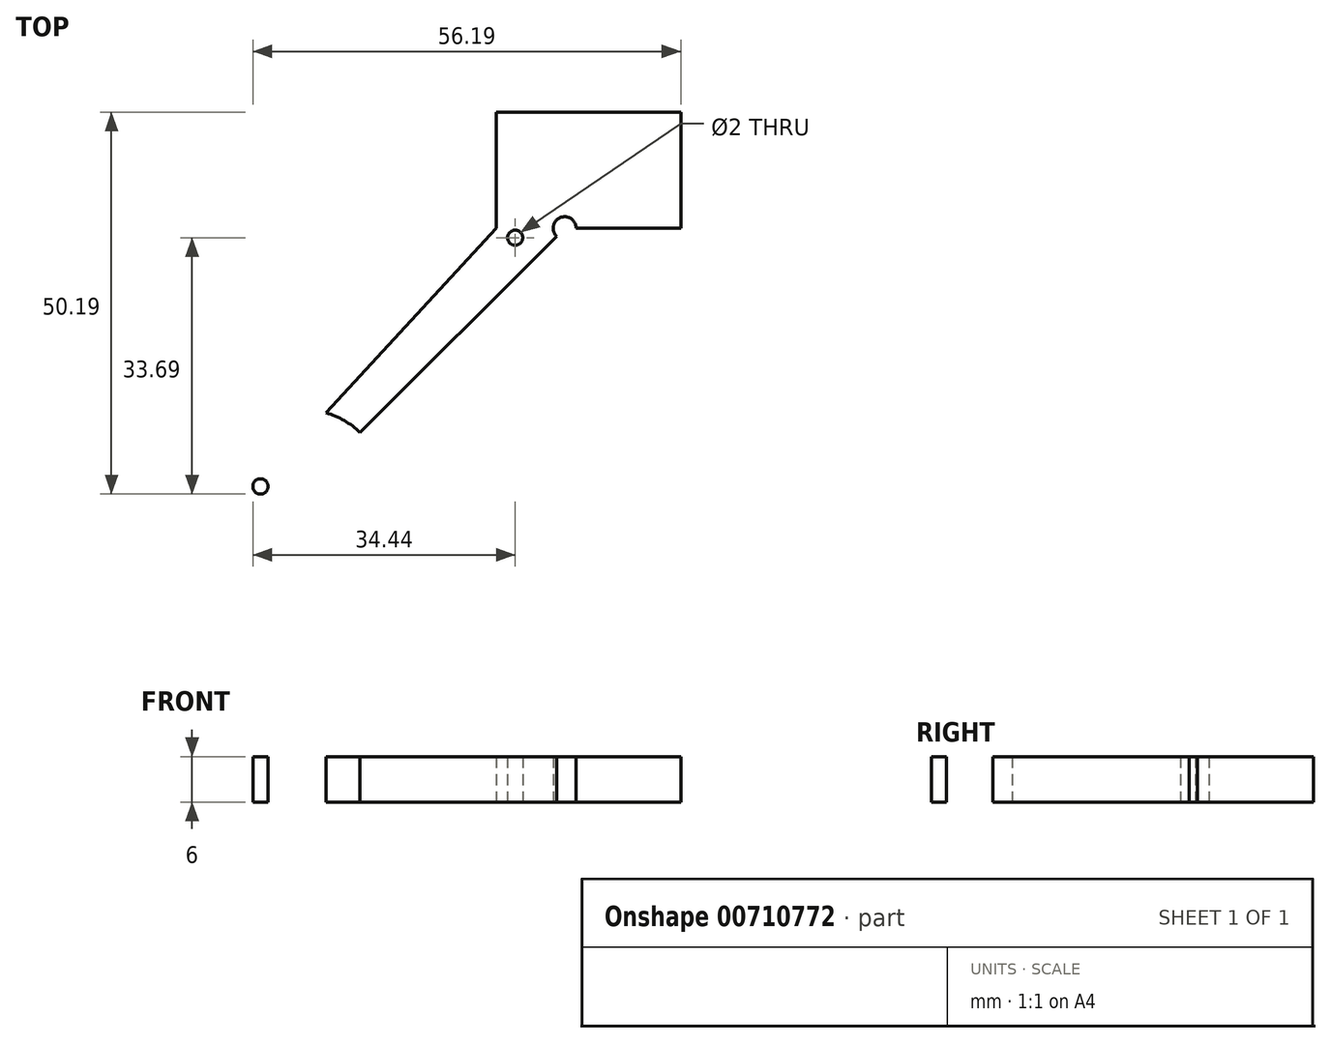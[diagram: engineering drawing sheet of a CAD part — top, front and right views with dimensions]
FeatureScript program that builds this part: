
annotation { "Feature Type Name" : "Feature", "Feature Type Description" : "" }
export const myFeature = defineFeature(function(context is Context, id is Id, definition is map)
    precondition{}
    {
        {
            var Q0;
            Q0=qCreatedBy(makeId("Top.planeOp"),FACE);
            var sketch = newSketch(context, id + "F0", { "sketchPlane" : qUnion([Q0])});
            skLineSegment(sketch, "E0.top", {"start": v(-15.25, -15.25) * mm, "end": v(-24.25, -15.25) * mm});
            skCircle(sketch, "E1.MirrorC", {"center": v(-55.2, -49.2) * mm, "radius": 1 * mm});
            skCircle(sketch, "E2.MirrorC", {"center": v(-43.2, -49.2) * mm, "radius": 1 * mm});
            skCircle(sketch, "E3.MirrorC", {"center": v(-49.2, -55.2) * mm, "radius": 1 * mm});
            skCircle(sketch, "E4.MirrorC", {"center": v(-49.2, -43.2) * mm, "radius": 1 * mm});
            skLineSegment(sketch, "E5.MirrorCS", {"start": v(-39.53, -46.6) * mm, "end": v(-8.18, -15.25) * mm});
            skLineSegment(sketch, "E6.MirrorCS", {"start": v(-46.6, -39.53) * mm, "end": v(-24.25, -15.25) * mm});
            skCircle(sketch, "E7.MirrorC", {"center": v(-49.2, -49.2) * mm, "radius": 10 * mm});
            skCircle(sketch, "E8.MirrorC", {"center": v(-49.2, -49.2) * mm, "radius": 2.5 * mm});
            skCircle(sketch, "E9", {"center": v(-15.25, -15.25) * mm, "radius": 1.5 * mm});
            skLineSegment(sketch, "E10", {"start": v(-24.25, -16.5) * mm, "end": v(-21.75, -16.5) * mm});
            skCircle(sketch, "E11", {"center": v(-21.75, -16.5) * mm, "radius": 1 * mm});
            skLineSegment(sketch, "E12.bottom", {"start": v(-24.25, -15.25) * mm, "end": v(0, -15.25) * mm});
            skLineSegment(sketch, "E12.top", {"start": v(-24.25, 0) * mm, "end": v(0, 0) * mm});
            skLineSegment(sketch, "E12.left", {"start": v(-24.25, -15.25) * mm, "end": v(-24.25, 0) * mm});
            skLineSegment(sketch, "E12.right", {"start": v(0, -15.25) * mm, "end": v(0, 0) * mm});
            skLineSegment(sketch, "E13", {"start": v(-49.2, -49.2) * mm, "end": v(-39.2, -49.2) * mm});
            skLineSegment(sketch, "E14", {"start": v(-39.2, -49.2) * mm, "end": v(-49.2, -49.2) * mm});
            skLineSegment(sketch, "E15", {"start": v(-59.2, -49.2) * mm, "end": v(-49.2, -49.2) * mm});
            skLineSegment(sketch, "E16", {"start": v(-49.2, -39.2) * mm, "end": v(-49.2, -59.2) * mm});
            skLineSegment(sketch, "E17", {"start": v(-15.25, -15.25) * mm, "end": v(-49.2, -49.2) * mm});
            skSolve(sketch);
        }
        {
            var Q0;
            Q0=makeQuery(id+"F0.imprint","IMPRINT",FACE,{"disambiguationData":[TD([[makeQuery(id+"F0.imprint","IMPRINT",EDGE,{"derivedFrom":sQuery(id+"F0.wireOp",EDGE,"2fc15603-6939-42b3-9b3e-9790c157a10a0.MirrorC")}),1.0]])]});
            var Q1;
            {var subQ5=sQuery(id+"F0.wireOp",EDGE,"2fc15603-6939-42b3-9b3e-9790c157a10a33.MirrorCS");Q1=makeQuery(id+"F0.imprint","IMPRINT",FACE,{"disambiguationData":[TD([[makeQuery(id+"F0.imprint","IMPRINT",EDGE,{"derivedFrom":subQ5}),-1.0]])]});}
            var Q2;
            {var subQ0=sQuery(id+"F0.wireOp",EDGE,"2fc15603-6939-42b3-9b3e-9790c157a10a26.MirrorCS");var subQ1=sQuery(id+"F0.wireOp",EDGE,"BjklgQHF-2lCu-BJus-xYrG-jcty17bZJsR9.bottom");var subQ2=makeQuery(id+"F0.imprint","INTERSECT",VERTEX,{"derivedFrom":[subQ1,subQ0]});Q2=makeQuery(id+"F0.imprint","IMPRINT",FACE,{"disambiguationData":[TD([[makeQuery(id+"F0.imprint","IMPRINT",EDGE,{"disambiguationData":[TD([[subQ2,-1.0]])],"derivedFrom":subQ1}),1.0]])]});}
            var Q3;
            {var subQ1=sQuery(id+"F0.wireOp",EDGE,"2fc15603-6939-42b3-9b3e-9790c157a10a22.MirrorCS");var subQ3=sQuery(id+"F0.wireOp",EDGE,"O8ek5n8F-vqc0-MOGU-3nzg-OkgxkjxWgx8A");var subQ4=makeQuery(id+"F0.imprint","INTERSECT",VERTEX,{"derivedFrom":[subQ1,subQ3]});Q3=makeQuery(id+"F0.imprint","IMPRINT",FACE,{"disambiguationData":[TD([[makeQuery(id+"F0.imprint","IMPRINT",EDGE,{"disambiguationData":[TD([[subQ4,1.0]])],"derivedFrom":subQ3}),-1.0]])]});}
            var Q4;
            {var subQ0=sQuery(id+"F0.wireOp",EDGE,"BjklgQHF-2lCu-BJus-xYrG-jcty17bZJsR9.bottom");var subQ8=makeQuery(id+"F0.imprint","INTERSECT",VERTEX,{"derivedFrom":[subQ0,sQuery(id+"F0.wireOp",EDGE,"T8tqe1wF-UkRa-UTp3-tCxK-rj2eIQjL2TSv")]});Q4=makeQuery(id+"F0.imprint","IMPRINT",FACE,{"disambiguationData":[TD([[makeQuery(id+"F0.imprint","IMPRINT",EDGE,{"disambiguationData":[TD([[subQ8,1.0]])],"derivedFrom":subQ0}),-1.0]])]});}
            var Q5;
            {var subQ3=sQuery(id+"F0.wireOp",EDGE,"QD21J1TR-R4I8-fKPh-C4il-LhPoGl2EDAA3");Q5=makeQuery(id+"F0.imprint","IMPRINT",FACE,{"disambiguationData":[TD([[makeQuery(id+"F0.imprint","IMPRINT",EDGE,{"derivedFrom":subQ3}),1.0]])]});}
            var Q6;
            Q6=makeQuery(id+"F0.imprint","IMPRINT",FACE,{"disambiguationData":[TD([[makeQuery(id+"F0.imprint","IMPRINT",EDGE,{"derivedFrom":sQuery(id+"F0.wireOp",EDGE,"G2xj0Bxy-JqKr-VXiR-P4dS-C8p4XoVfQqo2")}),-1.0]])]});
            var Q7;
            {var subQ1=sQuery(id+"F0.wireOp",EDGE,"E0.bottom");var subQ3=sQuery(id+"F0.wireOp",EDGE,"PJjClM9O-XOP3-8SZ1-1YEl-zbY6ReYBc9Jh");var subQ4=makeQuery(id+"F0.imprint","INTERSECT",VERTEX,{"derivedFrom":[subQ1,subQ3]});Q7=makeQuery(id+"F0.imprint","IMPRINT",FACE,{"disambiguationData":[TD([[makeQuery(id+"F0.imprint","IMPRINT",EDGE,{"disambiguationData":[TD([[subQ4,-1.0]])],"derivedFrom":subQ3}),-1.0]])]});}
            var Q8;
            {var subQ5=sQuery(id+"F0.wireOp",EDGE,"BjklgQHF-2lCu-BJus-xYrG-jcty17bZJsR9.bottom");var subQ7=sQuery(id+"F0.wireOp",EDGE,"T8tqe1wF-UkRa-UTp3-tCxK-rj2eIQjL2TSv");var subQ8=makeQuery(id+"F0.imprint","INTERSECT",VERTEX,{"derivedFrom":[subQ5,subQ7]});Q8=makeQuery(id+"F0.imprint","IMPRINT",FACE,{"disambiguationData":[TD([[makeQuery(id+"F0.imprint","IMPRINT",EDGE,{"disambiguationData":[TD([[subQ8,1.0]])],"derivedFrom":subQ5}),1.0]])]});}
            var Q9;
            {var subQ3=sQuery(id+"F0.wireOp",EDGE,"E0.left");var subQ7=sQuery(id+"F0.wireOp",EDGE,"PJjClM9O-XOP3-8SZ1-1YEl-zbY6ReYBc9Jh");var subQ9=makeQuery(id+"F0.imprint","INTERSECT",VERTEX,{"derivedFrom":[subQ3,subQ7]});Q9=makeQuery(id+"F0.imprint","IMPRINT",FACE,{"disambiguationData":[TD([[makeQuery(id+"F0.imprint","IMPRINT",EDGE,{"disambiguationData":[TD([[subQ9,-1.0]])],"derivedFrom":subQ3}),-1.0]])]});}
            var Q10;
            {var subQ0=sQuery(id+"F0.wireOp",EDGE,"PJjClM9O-XOP3-8SZ1-1YEl-zbY6ReYBc9Jh");var subQ1=sQuery(id+"F0.wireOp",EDGE,"E0.left");var subQ2=makeQuery(id+"F0.imprint","INTERSECT",VERTEX,{"derivedFrom":[subQ1,subQ0]});Q10=makeQuery(id+"F0.imprint","IMPRINT",FACE,{"disambiguationData":[TD([[makeQuery(id+"F0.imprint","IMPRINT",EDGE,{"disambiguationData":[TD([[subQ2,-1.0]])],"derivedFrom":subQ1}),1.0]])]});}
            var Q11;
            {var subQ1=sQuery(id+"F0.wireOp",EDGE,"E0.left");var subQ9=sQuery(id+"F0.wireOp",EDGE,"4uT9bfEZ-qlL9-jcBX-Nhsu-rmtl1X7BlQzy");var subQ11=makeQuery(id+"F0.imprint","INTERSECT",VERTEX,{"derivedFrom":[subQ1,subQ9]});Q11=makeQuery(id+"F0.imprint","IMPRINT",FACE,{"disambiguationData":[TD([[makeQuery(id+"F0.imprint","IMPRINT",EDGE,{"disambiguationData":[TD([[subQ11,-1.0]])],"derivedFrom":subQ1}),1.0]])]});}
            var Q12;
            {var subQ0=sQuery(id+"F0.wireOp",EDGE,"4uT9bfEZ-qlL9-jcBX-Nhsu-rmtl1X7BlQzy");var subQ3=sQuery(id+"F0.wireOp",EDGE,"E0.left");var subQ4=makeQuery(id+"F0.imprint","INTERSECT",VERTEX,{"derivedFrom":[subQ3,subQ0]});Q12=makeQuery(id+"F0.imprint","IMPRINT",FACE,{"disambiguationData":[TD([[makeQuery(id+"F0.imprint","IMPRINT",EDGE,{"disambiguationData":[TD([[subQ4,-1.0]])],"derivedFrom":subQ3}),-1.0]])]});}
            var Q13;
            {var subQ0=sQuery(id+"F0.wireOp",EDGE,"zzauZid5-o7Uc-fnxz-2Q5N-lc55jAUrYsHn");Q13=makeQuery(id+"F0.imprint","IMPRINT",FACE,{"disambiguationData":[TD([[makeQuery(id+"F0.imprint","IMPRINT",EDGE,{"derivedFrom":subQ0}),-1.0]])]});}
            var Q14;
            {var subQ0=sQuery(id+"F0.wireOp",EDGE,"oEed2lwB-LAN2-I5ee-bfS7-ysMyHjfk99YW");Q14=makeQuery(id+"F0.imprint","IMPRINT",FACE,{"disambiguationData":[TD([[makeQuery(id+"F0.imprint","IMPRINT",EDGE,{"derivedFrom":subQ0}),-1.0]])]});}
            var Q15;
            {var subQ3=sQuery(id+"F0.wireOp",EDGE,"ZsRWKTD2-uWTc-TLXd-d7Hk-2En77BC8SWwa");Q15=makeQuery(id+"F0.imprint","IMPRINT",FACE,{"disambiguationData":[TD([[makeQuery(id+"F0.imprint","IMPRINT",EDGE,{"derivedFrom":subQ3}),1.0]])]});}
            var Q16;
            {var subQ0=sQuery(id+"F0.wireOp",EDGE,"2fc15603-6939-42b3-9b3e-9790c157a10a34.MirrorCS");Q16=makeQuery(id+"F0.imprint","IMPRINT",FACE,{"disambiguationData":[TD([[makeQuery(id+"F0.imprint","IMPRINT",EDGE,{"derivedFrom":subQ0}),-1.0]])]});}
            var Q17;
            Q17=makeQuery(id+"F0.imprint","IMPRINT",FACE,{"disambiguationData":[TD([[makeQuery(id+"F0.imprint","IMPRINT",EDGE,{"derivedFrom":sQuery(id+"F0.wireOp",EDGE,"2fc15603-6939-42b3-9b3e-9790c157a10a1.MirrorC")}),-1.0]])]});
            var Q18;
            {var subQ1=sQuery(id+"F0.wireOp",EDGE,"BjklgQHF-2lCu-BJus-xYrG-jcty17bZJsR9.top");var subQ7=sQuery(id+"F0.wireOp",EDGE,"E5.MirrorCS");var subQ8=makeQuery(id+"F0.imprint","INTERSECT",VERTEX,{"derivedFrom":[subQ1,subQ7]});Q18=makeQuery(id+"F0.imprint","IMPRINT",FACE,{"disambiguationData":[TD([[makeQuery(id+"F0.imprint","IMPRINT",EDGE,{"disambiguationData":[TD([[subQ8,1.0]])],"derivedFrom":subQ1}),-1.0]])]});}
            var Q19;
            {var subQ5=sQuery(id+"F0.wireOp",EDGE,"E6.MirrorCS");Q19=makeQuery(id+"F0.imprint","IMPRINT",FACE,{"disambiguationData":[TD([[makeQuery(id+"F0.imprint","IMPRINT",EDGE,{"derivedFrom":subQ5}),-1.0]])]});}
            var Q20;
            Q20=makeQuery(id+"F0.imprint","IMPRINT",FACE,{"disambiguationData":[TD([[makeQuery(id+"F0.imprint","IMPRINT",EDGE,{"derivedFrom":sQuery(id+"F0.wireOp",EDGE,"E1.MirrorC")}),1.0]])]});
            var Q21;
            {var subQ0=sQuery(id+"F0.wireOp",EDGE,"BjklgQHF-2lCu-BJus-xYrG-jcty17bZJsR9.top");var subQ4=makeQuery(id+"F0.imprint","INTERSECT",VERTEX,{"derivedFrom":[subQ0,sQuery(id+"F0.wireOp",EDGE,"E5.MirrorCS")]});Q21=makeQuery(id+"F0.imprint","IMPRINT",FACE,{"disambiguationData":[TD([[makeQuery(id+"F0.imprint","IMPRINT",EDGE,{"disambiguationData":[TD([[subQ4,1.0]])],"derivedFrom":subQ0}),1.0]])]});}
            var Q22;
            {var subQ1=sQuery(id+"F0.wireOp",EDGE,"2fc15603-6939-42b3-9b3e-9790c157a10a29.MirrorCS");var subQ3=sQuery(id+"F0.wireOp",EDGE,"nAFaoFor-0JIV-fJh0-xI6d-kOEGwFpFNsGw");var subQ4=makeQuery(id+"F0.imprint","INTERSECT",VERTEX,{"derivedFrom":[subQ1,subQ3]});Q22=makeQuery(id+"F0.imprint","IMPRINT",FACE,{"disambiguationData":[TD([[makeQuery(id+"F0.imprint","IMPRINT",EDGE,{"disambiguationData":[TD([[subQ4,-1.0]])],"derivedFrom":subQ3}),-1.0]])]});}
            var Q23;
            {var subQ1=sQuery(id+"F0.wireOp",EDGE,"E0.top");var subQ3=sQuery(id+"F0.wireOp",EDGE,"E9");var subQ4=makeQuery(id+"F0.imprint","INTERSECT",VERTEX,{"derivedFrom":[subQ1,subQ3]});Q23=makeQuery(id+"F0.imprint","IMPRINT",FACE,{"disambiguationData":[TD([[makeQuery(id+"F0.imprint","IMPRINT",EDGE,{"disambiguationData":[TD([[subQ4,1.0]])],"derivedFrom":subQ3}),-1.0]])]});}
            extrude(context, id + "F1", {"entities" : qUnion([Q0, Q1, Q2, Q3, Q4, Q5, Q6, Q7, Q8, Q9, Q10, Q11, Q12, Q13, Q14, Q15, Q16, Q17, Q18, Q19, Q20, Q21, Q22, Q23]), "depth" : 6 * mm, "offsetDistance" : 25 * mm});
        }
    });
